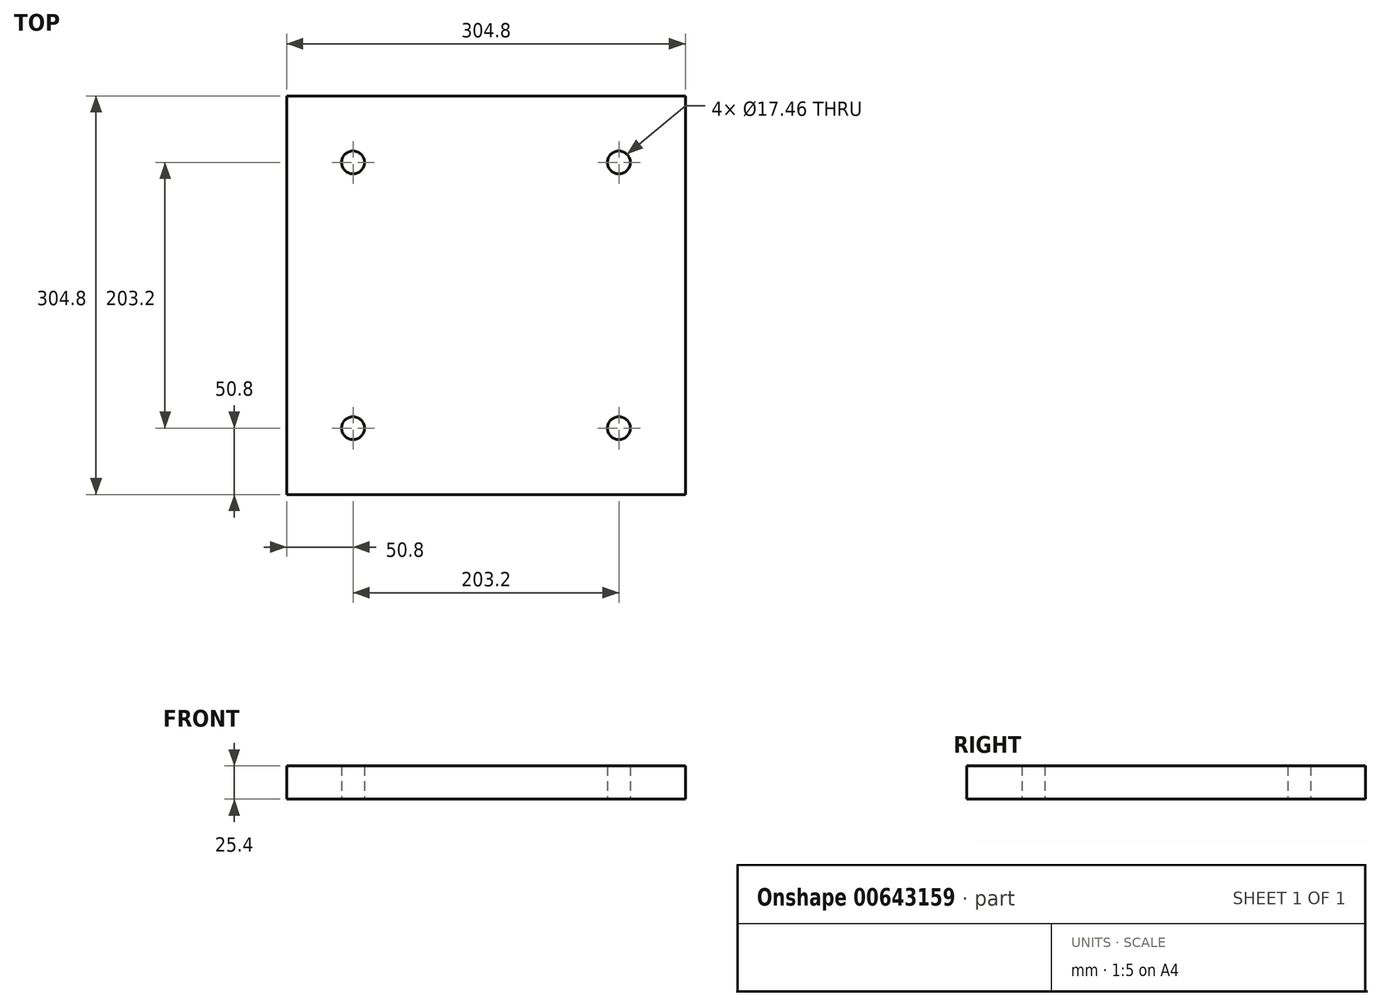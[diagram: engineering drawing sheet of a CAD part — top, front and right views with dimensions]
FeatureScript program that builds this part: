
annotation { "Feature Type Name" : "Feature", "Feature Type Description" : "" }
export const myFeature = defineFeature(function(context is Context, id is Id, definition is map)
    precondition{}
    {
        {
            var Q0;
            Q0=qCreatedBy(makeId("Top.planeOp"),FACE);
            var sketch = newSketch(context, id + "F0", { "sketchPlane" : qUnion([Q0])});
            skLineSegment(sketch, "E0.bottom", {"start": v(152.4, -152.4) * mm, "end": v(-152.4, -152.4) * mm});
            skLineSegment(sketch, "E0.top", {"start": v(152.4, 152.4) * mm, "end": v(-152.4, 152.4) * mm});
            skLineSegment(sketch, "E0.left", {"start": v(152.4, -152.4) * mm, "end": v(152.4, 152.4) * mm});
            skLineSegment(sketch, "E0.right", {"start": v(-152.4, -152.4) * mm, "end": v(-152.4, 152.4) * mm});
            skPoint(sketch, "E0.middle", {"position": v(0, 0) * mm});
            skCircle(sketch, "E1", {"center": v(-101.6, 101.6) * mm, "radius": 8.73 * mm});
            skCircle(sketch, "E2.MirrorC", {"center": v(101.6, 101.6) * mm, "radius": 8.73 * mm});
            skCircle(sketch, "E3.MirrorC", {"center": v(-101.6, -101.6) * mm, "radius": 8.73 * mm});
            skCircle(sketch, "E4.MirrorC", {"center": v(101.6, -101.6) * mm, "radius": 8.73 * mm});
            skSolve(sketch);
        }
        {
            var Q0;
            Q0 = qSketchRegion(id + "F0", true);
            extrude(context, id + "F1", {"entities" : qUnion([Q0]), "depth" : 25.4 * mm, "offsetDistance" : 25.4 * mm});
        }
    });
